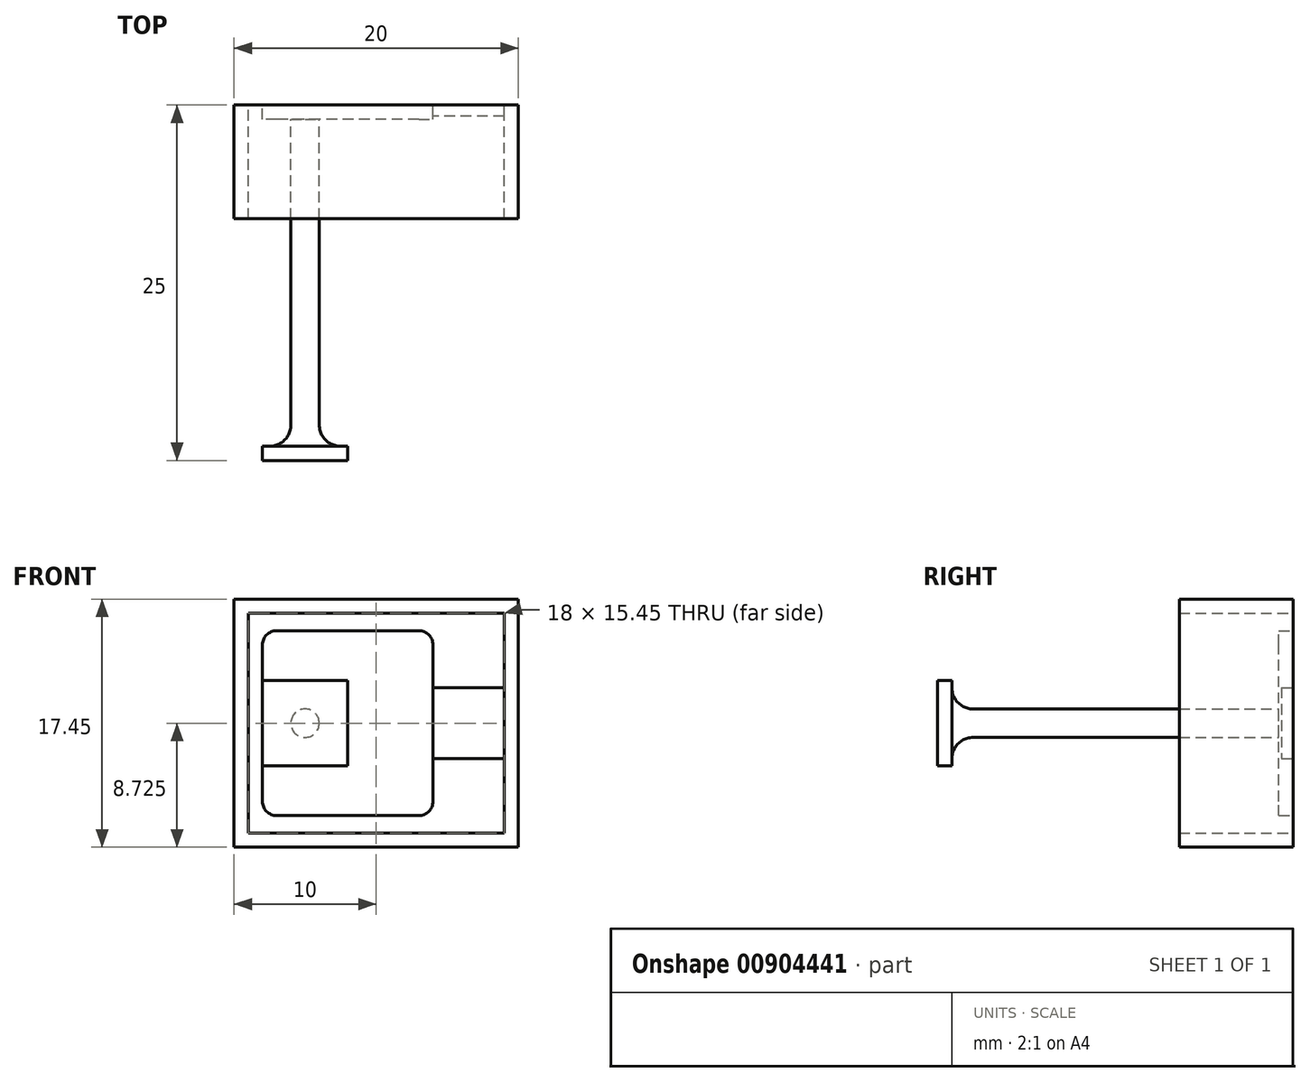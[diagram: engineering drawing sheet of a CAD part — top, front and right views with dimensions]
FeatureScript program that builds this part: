
annotation { "Feature Type Name" : "Feature", "Feature Type Description" : "" }
export const myFeature = defineFeature(function(context is Context, id is Id, definition is map)
    precondition{}
    {
        {
            var Q0;
            Q0=qCreatedBy(makeId("Front.planeOp"),FACE);
            var sketch = newSketch(context, id + "F0", { "sketchPlane" : qUnion([Q0])});
            skLineSegment(sketch, "E0", {"start": v(0, 17.45) * mm, "end": v(0, 0) * mm});
            skLineSegment(sketch, "E1", {"start": v(0, 0) * mm, "end": v(20, 0) * mm});
            skLineSegment(sketch, "E2", {"start": v(20, 0) * mm, "end": v(20, 17.45) * mm});
            skLineSegment(sketch, "E3", {"start": v(20, 17.45) * mm, "end": v(0, 17.45) * mm});
            skLineSegment(sketch, "E4", {"start": v(14, 11.23) * mm, "end": v(14, 15.23) * mm});
            skLineSegment(sketch, "E5", {"start": v(14, 15.23) * mm, "end": v(2, 15.23) * mm});
            skLineSegment(sketch, "E6", {"start": v(2, 2.22) * mm, "end": v(14, 2.22) * mm});
            skLineSegment(sketch, "E7", {"start": v(14, 2.22) * mm, "end": v(14, 6.22) * mm});
            skLineSegment(sketch, "E8", {"start": v(19, 6.22) * mm, "end": v(19, 1) * mm});
            skLineSegment(sketch, "E9", {"start": v(1, 1) * mm, "end": v(1, 16.45) * mm});
            skLineSegment(sketch, "E10", {"start": v(19, 16.45) * mm, "end": v(19, 11.23) * mm});
            skLineSegment(sketch, "E11", {"start": v(19, 16.45) * mm, "end": v(1, 16.45) * mm});
            skLineSegment(sketch, "E12", {"start": v(1, 1) * mm, "end": v(19, 1) * mm});
            skLineSegment(sketch, "E13", {"start": v(19, 6.22) * mm, "end": v(14, 6.22) * mm});
            skLineSegment(sketch, "E14", {"start": v(19, 11.23) * mm, "end": v(14, 11.23) * mm});
            skLineSegment(sketch, "E15", {"start": v(2, 15.23) * mm, "end": v(2, 2.22) * mm});
            skLineSegment(sketch, "E16", {"start": v(19, 11.23) * mm, "end": v(19, 6.22) * mm});
            skLineSegment(sketch, "E17", {"start": v(2, 11.72) * mm, "end": v(8, 11.72) * mm});
            skLineSegment(sketch, "E18", {"start": v(8, 11.72) * mm, "end": v(8, 5.72) * mm});
            skLineSegment(sketch, "E19", {"start": v(8, 5.72) * mm, "end": v(2, 5.72) * mm});
            skCircle(sketch, "E20", {"center": v(5, 8.72) * mm, "radius": 1 * mm});
            skPoint(sketch, "E20.centerSnap0", {"position": v(1, 8.72) * mm});
            skLineSegment(sketch, "E21", {"start": v(2, 11.72) * mm, "end": v(8, 5.72) * mm, "construction": true});
            skLineSegment(sketch, "E22", {"start": v(5, 8.72) * mm, "end": v(19, 8.72) * mm, "construction": true});
            skSolve(sketch);
        }
        {
            var Q0;
            Q0=qSketchRegion(id+"F0",true);
            extrude(context, id + "F1", {"entities" : qUnion([Q0]), "depth" : 8 * mm, "offsetDistance" : 25.4 * mm});
        }
        {
            var Q0;
            Q0=makeQuery(id+"F0.imprint","IMPRINT",FACE,{"disambiguationData":[TD([[makeQuery(id+"F0.imprint","IMPRINT",EDGE,{"derivedFrom":sQuery(id+"F0.wireOp",EDGE,"E4")}),1.0]])]});
            var Q1;
            {var subQ0=sQuery(id+"F0.wireOp",EDGE,"E17");Q1=makeQuery(id+"F0.imprint","IMPRINT",FACE,{"disambiguationData":[TD([[makeQuery(id+"F0.imprint","IMPRINT",EDGE,{"derivedFrom":subQ0}),-1.0]])]});}
            extrude(context, id + "F2", {"entities" : qUnion([Q0, Q1]), "operationType" : NewBodyOperationType.ADD, "depth" : 1 * mm, "offsetDistance" : 25 * mm});
        }
        {
            var Q0;
            Q0=makeQuery(id+"F0.imprint","IMPRINT",FACE,{"disambiguationData":[TD([[makeQuery(id+"F0.imprint","IMPRINT",EDGE,{"derivedFrom":sQuery(id+"F0.wireOp",EDGE,"E20")}),1.0]])]});
            extrude(context, id + "F3", {"entities" : qUnion([Q0]), "operationType" : NewBodyOperationType.ADD, "depth" : 25 * mm, "offsetDistance" : 25 * mm});
        }
        {
            var Q0;
            Q0=makeQuery(id+"F3.opExtrude","CAP_FACE",FACE,{"disambiguationData":[OSD([sQuery(id+"F0.wireOp",EDGE,"E20")])],"isStart":false});
            var sketch = newSketch(context, id + "F4", { "sketchPlane" : qUnion([Q0])});
            skLineSegment(sketch, "E23.bottom", {"start": v(2, 11.72) * mm, "end": v(8, 11.73) * mm});
            skLineSegment(sketch, "E23.top", {"start": v(2, 5.73) * mm, "end": v(8, 5.73) * mm});
            skLineSegment(sketch, "E23.left", {"start": v(2, 11.72) * mm, "end": v(2, 5.73) * mm});
            skLineSegment(sketch, "E23.right", {"start": v(8, 11.73) * mm, "end": v(8, 5.73) * mm});
            skPoint(sketch, "E23.middle", {"position": v(5, 8.72) * mm});
            skSolve(sketch);
        }
        {
            var Q0;
            Q0=qSketchRegion(id+"F4",true);
            extrude(context, id + "F5", {"entities" : qUnion([Q0]), "operationType" : NewBodyOperationType.ADD, "oppositeDirection" : true, "depth" : 1 * mm, "offsetDistance" : 25 * mm});
        }
        {
            var Q0;
            Q0=makeQuery(id+"F5.boolean.opBoolean","INTERSECT",EDGE,{"derivedFrom":[makeQuery(id+"F3.opExtrude","SWEPT_FACE",FACE,{"disambiguationData":[OSD([sQuery(id+"F0.wireOp",EDGE,"E20")])]}),makeQuery(id+"F5.opExtrude","CAP_FACE",FACE,{"disambiguationData":[OSD([sQuery(id+"F4.wireOp",EDGE,"E23.bottom"),sQuery(id+"F4.wireOp",EDGE,"E23.top"),sQuery(id+"F4.wireOp",EDGE,"E23.left"),sQuery(id+"F4.wireOp",EDGE,"E23.right")])],"isStart":false})]});
            var Q1;
            Q1=makeQuery(id+"F2.opExtrude","CAP_EDGE",EDGE,{"disambiguationData":[OSD([sQuery(id+"F0.wireOp",EDGE,"E20")])],"isStart":false});
            fillet(context, id + "F6", {"entities" : qUnion([Q0, Q1]), "radius" : 1.5 * mm, "tangentPropagation" : true, "allowEdgeOverflow" : false});
        }
        {
            var Q0;
            Q0=makeQuery(id+"F2.opExtrude","CAP_FACE",FACE,{"disambiguationData":[OSD([sQuery(id+"F0.wireOp",EDGE,"E4"),sQuery(id+"F0.wireOp",EDGE,"E5"),sQuery(id+"F0.wireOp",EDGE,"E6"),sQuery(id+"F0.wireOp",EDGE,"E7"),sQuery(id+"F0.wireOp",EDGE,"E13"),sQuery(id+"F0.wireOp",EDGE,"E14"),sQuery(id+"F0.wireOp",EDGE,"E15"),sQuery(id+"F0.wireOp",EDGE,"E16"),sQuery(id+"F0.wireOp",EDGE,"E20")])],"isStart":false});
            var sketch = newSketch(context, id + "F7", { "sketchPlane" : qUnion([Q0])});
            skLineSegment(sketch, "E24.bottom", {"start": v(14, 11.23) * mm, "end": v(19, 11.23) * mm});
            skLineSegment(sketch, "E24.top", {"start": v(14, 6.22) * mm, "end": v(19, 6.22) * mm});
            skLineSegment(sketch, "E24.left", {"start": v(14, 11.23) * mm, "end": v(14, 6.22) * mm});
            skLineSegment(sketch, "E24.right", {"start": v(19, 11.23) * mm, "end": v(19, 6.22) * mm});
            skSolve(sketch);
        }
        {
            var Q0;
            Q0=qSketchRegion(id+"F7",true);
            extrude(context, id + "F8", {"entities" : qUnion([Q0]), "operationType" : NewBodyOperationType.REMOVE, "oppositeDirection" : true, "depth" : 0.2 * mm, "offsetDistance" : 25 * mm});
        }
        {
            var Q0;
            Q0=makeQuery(id+"F2.opExtrude","SWEPT_EDGE",EDGE,{"disambiguationData":[OSD([sQuery(id+"F0.wireOp",EDGE,"E5"),sQuery(id+"F0.wireOp",EDGE,"E15")])]});
            var Q1;
            Q1=makeQuery(id+"F2.opExtrude","SWEPT_EDGE",EDGE,{"disambiguationData":[OSD([sQuery(id+"F0.wireOp",EDGE,"E4"),sQuery(id+"F0.wireOp",EDGE,"E5")])]});
            var Q2;
            Q2=makeQuery(id+"F2.opExtrude","SWEPT_EDGE",EDGE,{"disambiguationData":[OSD([sQuery(id+"F0.wireOp",EDGE,"E6"),sQuery(id+"F0.wireOp",EDGE,"E15")])]});
            var Q3;
            Q3=makeQuery(id+"F2.opExtrude","SWEPT_EDGE",EDGE,{"disambiguationData":[OSD([sQuery(id+"F0.wireOp",EDGE,"E6"),sQuery(id+"F0.wireOp",EDGE,"E7")])]});
            fillet(context, id + "F9", {"entities" : qUnion([Q0, Q1, Q2, Q3]), "radius" : 1 * mm, "tangentPropagation" : true, "allowEdgeOverflow" : false});
        }
    });
